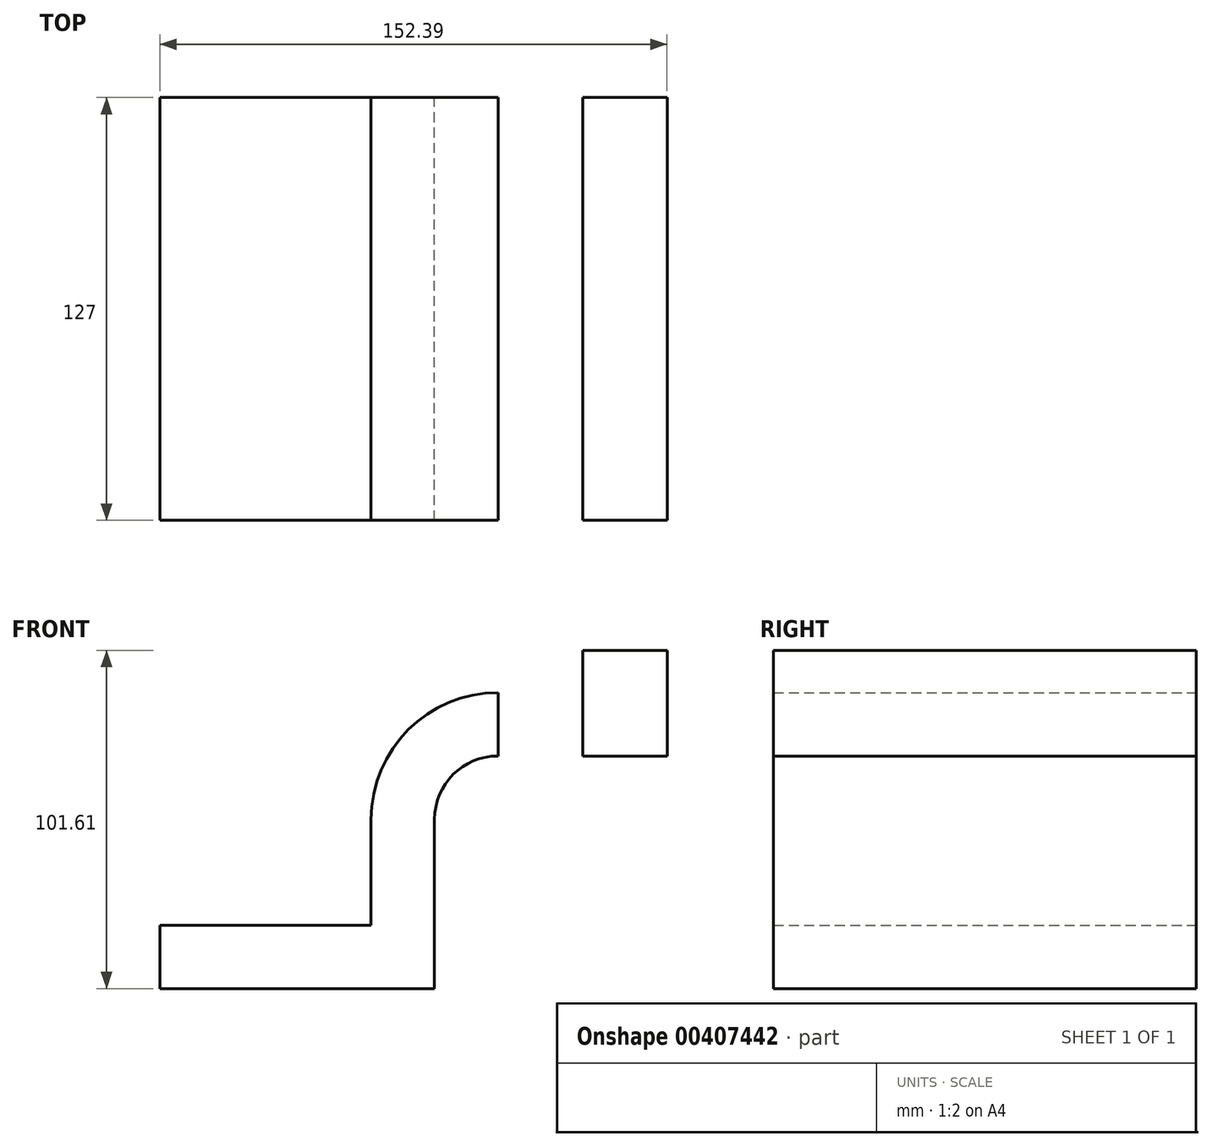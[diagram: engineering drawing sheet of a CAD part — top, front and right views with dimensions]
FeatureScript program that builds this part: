
annotation { "Feature Type Name" : "Feature", "Feature Type Description" : "" }
export const myFeature = defineFeature(function(context is Context, id is Id, definition is map)
    precondition{}
    {
        {
            var Q0;
            Q0=qCreatedBy(makeId("Front.planeOp"),FACE);
            var sketch = newSketch(context, id + "F0", { "sketchPlane" : qUnion([Q0])});
            skLineSegment(sketch, "E0.bottom", {"start": v(-41.28, -9.53) * mm, "end": v(41.28, -9.53) * mm});
            skLineSegment(sketch, "E0.top", {"start": v(-41.28, 9.53) * mm, "end": v(41.28, 9.53) * mm});
            skLineSegment(sketch, "E0.left", {"start": v(-41.28, -9.53) * mm, "end": v(-41.28, 9.53) * mm});
            skLineSegment(sketch, "E0.right", {"start": v(41.28, -9.53) * mm, "end": v(41.28, 9.53) * mm});
            skPoint(sketch, "E0.middle", {"position": v(0, 0) * mm});
            skLineSegment(sketch, "E1.bottom", {"start": v(111.12, 92.07) * mm, "end": v(60.32, 92.07) * mm});
            skLineSegment(sketch, "E1.top", {"start": v(111.12, 60.32) * mm, "end": v(60.32, 60.32) * mm});
            skLineSegment(sketch, "E1.left", {"start": v(111.12, 92.08) * mm, "end": v(111.12, 60.32) * mm});
            skLineSegment(sketch, "E1.right", {"start": v(60.32, 92.08) * mm, "end": v(60.32, 60.32) * mm});
            skPoint(sketch, "E1.middle", {"position": v(85.72, 76.2) * mm});
            skLineSegment(sketch, "E2", {"start": v(41.28, 9.53) * mm, "end": v(41.28, 41.27) * mm});
            skArc(sketch, "E3", {"start": v(41.27, 41.27) * mm, "mid": v(46.85, 54.75) * mm, "end": v(60.32, 60.33) * mm});
            skLineSegment(sketch, "E4", {"start": v(60.32, 60.32) * mm, "end": v(85.72, 60.32) * mm});
            skArc(sketch, "E5.0", {"start": v(22.22, 41.27) * mm, "mid": v(33.38, 68.22) * mm, "end": v(60.32, 79.38) * mm});
            skLineSegment(sketch, "E5.1", {"start": v(22.22, 9.53) * mm, "end": v(22.22, 41.27) * mm});
            skLineSegment(sketch, "E6", {"start": v(85.72, 60.32) * mm, "end": v(85.72, 92.07) * mm});
            skFitSpline(sketch, "E7", {"points": [v(-41.28, 9.53) * mm, v(60.32, 79.38) * mm], "startDerivative": vector(20.51, 117.31) * mm, "endDerivative": vector(180.97, -8.8) * mm});
            skSolve(sketch);
        }
        {
            var Q0;
            {var subQ0=sQuery(id+"F0.wireOp",EDGE,"E2");Q0=makeQuery(id+"F0.imprint","IMPRINT",FACE,{"disambiguationData":[TD([[makeQuery(id+"F0.imprint","IMPRINT",EDGE,{"derivedFrom":subQ0}),1.0]])]});}
            var Q1;
            Q1=makeQuery(id+"F0.imprint","IMPRINT",FACE,{"disambiguationData":[TD([[makeQuery(id+"F0.imprint","IMPRINT",EDGE,{"derivedFrom":sQuery(id+"F0.wireOp",EDGE,"E5.0")}),1.0]])]});
            var Q2;
            {var subQ0=sQuery(id+"F0.wireOp",EDGE,"E4");Q2=makeQuery(id+"F0.imprint","IMPRINT",FACE,{"disambiguationData":[TD([[makeQuery(id+"F0.imprint","IMPRINT",EDGE,{"derivedFrom":subQ0}),1.0]])]});}
            var Q3;
            Q3=makeQuery(id+"F0.imprint","IMPRINT",FACE,{"disambiguationData":[TD([[makeQuery(id+"F0.imprint","IMPRINT",EDGE,{"derivedFrom":sQuery(id+"F0.wireOp",EDGE,"E1.top")}),-1.0]])]});
            var Q4;
            Q4=makeQuery(id+"F0.imprint","IMPRINT",FACE,{"disambiguationData":[TD([[makeQuery(id+"F0.imprint","IMPRINT",EDGE,{"derivedFrom":sQuery(id+"F0.wireOp",EDGE,"E0.bottom")}),1.0]])]});
            extrude(context, id + "F1", {"entities" : qUnion([Q0, Q1, Q2, Q3, Q4]), "endBound" : BoundingType.SYMMETRIC, "depth" : 127 * mm});
        }
    });
